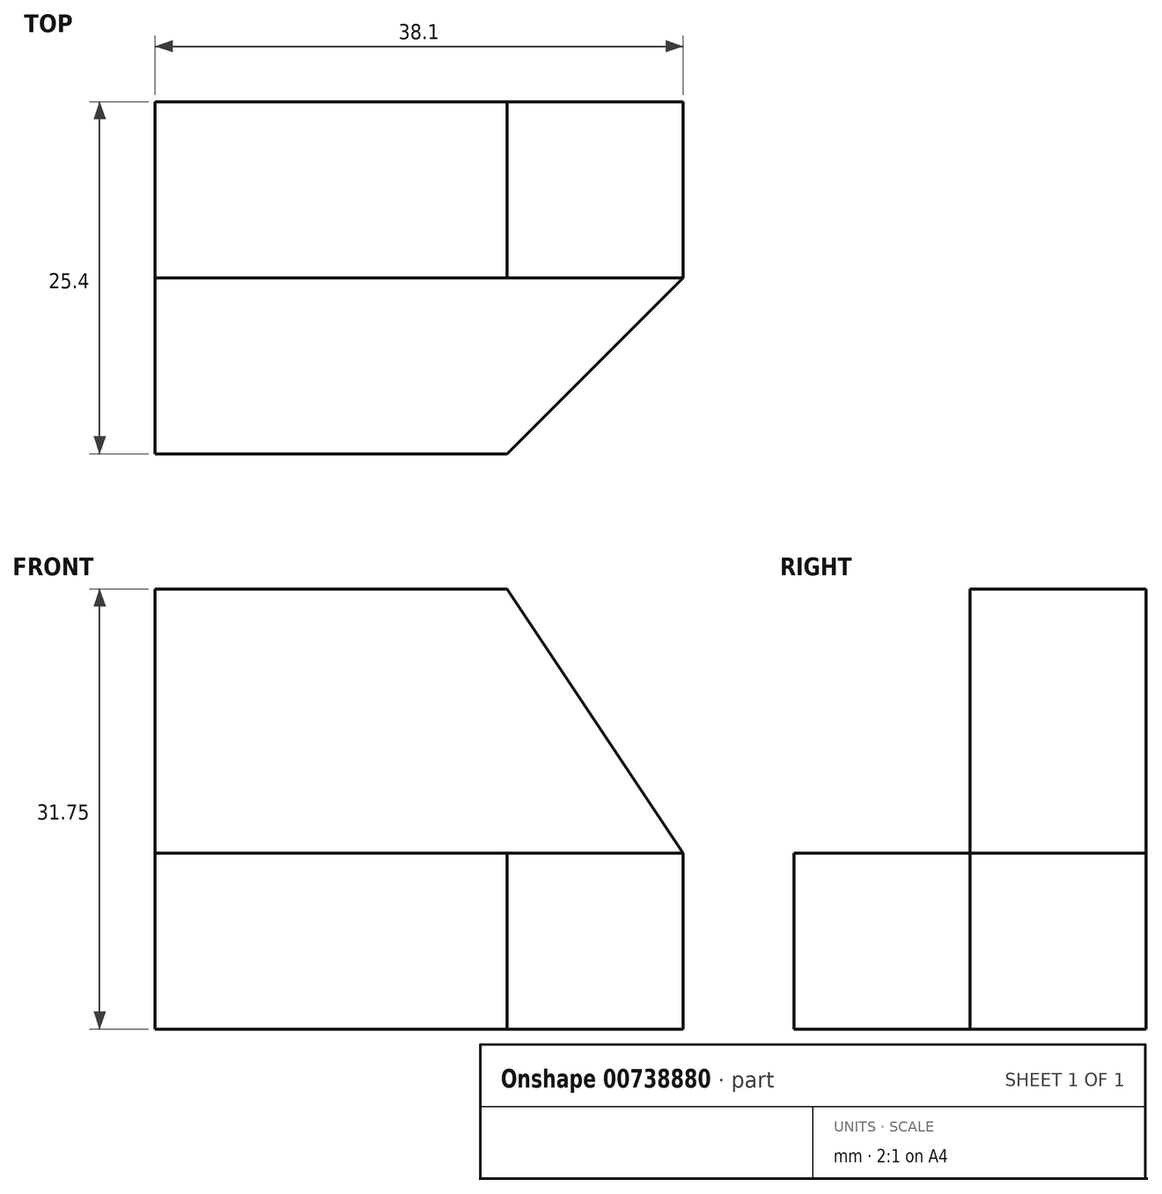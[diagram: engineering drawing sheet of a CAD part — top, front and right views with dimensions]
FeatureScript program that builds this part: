
annotation { "Feature Type Name" : "Feature", "Feature Type Description" : "" }
export const myFeature = defineFeature(function(context is Context, id is Id, definition is map)
    precondition{}
    {
        {
            var Q0;
            Q0=qCreatedBy(makeId("Front.planeOp"),FACE);
            var sketch = newSketch(context, id + "F0", { "sketchPlane" : qUnion([Q0])});
            skLineSegment(sketch, "E0", {"start": v(0, 0) * mm, "end": v(0, 31.75) * mm});
            skLineSegment(sketch, "E1", {"start": v(0, 31.75) * mm, "end": v(38.1, 31.75) * mm});
            skLineSegment(sketch, "E2", {"start": v(38.1, 31.75) * mm, "end": v(38.1, 0) * mm});
            skLineSegment(sketch, "E3", {"start": v(38.1, 0) * mm, "end": v(0, 0) * mm});
            skSolve(sketch);
        }
        {
            var Q0;
            Q0=makeQuery(id+"F0.imprint","IMPRINT",FACE,{"disambiguationData":[TD([[makeQuery(id+"F0.imprint","IMPRINT",EDGE,{"derivedFrom":sQuery(id+"F0.wireOp",EDGE,"E0")}),-1.0]])]});
            extrude(context, id + "F1", {"entities" : qUnion([Q0]), "depth" : 25.4 * mm, "offsetDistance" : 25.4 * mm});
        }
        {
            var Q0;
            Q0=makeQuery(id+"F1.opExtrude","SWEPT_FACE",FACE,{"disambiguationData":[OSD([sQuery(id+"F0.wireOp",EDGE,"E2")])]});
            var sketch = newSketch(context, id + "F2", { "sketchPlane" : qUnion([Q0])});
            skLineSegment(sketch, "E4", {"start": v(-12.7, 31.75) * mm, "end": v(-12.7, 12.7) * mm});
            skLineSegment(sketch, "E5", {"start": v(-12.7, 12.7) * mm, "end": v(-25.4, 12.7) * mm});
            skSolve(sketch);
        }
        {
            var Q0;
            Q0 = qSketchRegion(id + "F2", true);
            var Q1;
            {var subQ0=sQuery(id+"F2.wireOp",EDGE,"E4");Q1=makeQuery(id+"F2.imprint","IMPRINT",FACE,{"disambiguationData":[TD([[makeQuery(id+"F2.imprint","IMPRINT",EDGE,{"derivedFrom":subQ0}),-1.0]])]});}
            extrude(context, id + "F3", {"entities" : qUnion([Q0, Q1]), "operationType" : NewBodyOperationType.REMOVE, "endBound" : BoundingType.THROUGH_ALL, "oppositeDirection" : true, "depth" : 25.4 * mm, "offsetDistance" : 25.4 * mm});
        }
        {
            var Q0;
            Q0=makeQuery(id+"F3.boolean.opBoolean","COPY",FACE,{"derivedFrom":makeQuery(id+"F3.opExtrude","SWEPT_FACE",FACE,{"disambiguationData":[OSD([sQuery(id+"F2.wireOp",EDGE,"E4")])]})});
            var sketch = newSketch(context, id + "F4", { "sketchPlane" : qUnion([Q0])});
            skLineSegment(sketch, "E6", {"start": v(25.4, 31.75) * mm, "end": v(38.1, 12.7) * mm});
            skSolve(sketch);
        }
        {
            var Q0;
            Q0 = qSketchRegion(id + "F4", true);
            var Q1;
            {var subQ0=sQuery(id+"F4.wireOp",EDGE,"E6");Q1=makeQuery(id+"F4.imprint","IMPRINT",FACE,{"disambiguationData":[TD([[makeQuery(id+"F4.imprint","IMPRINT",EDGE,{"derivedFrom":subQ0}),1.0]])]});}
            extrude(context, id + "F5", {"entities" : qUnion([Q0, Q1]), "operationType" : NewBodyOperationType.REMOVE, "endBound" : BoundingType.THROUGH_ALL, "oppositeDirection" : true, "depth" : 25.4 * mm, "offsetDistance" : 25.4 * mm});
        }
        {
            var Q0;
            Q0=makeQuery(id+"F3.boolean.opBoolean","COPY",FACE,{"derivedFrom":makeQuery(id+"F3.opExtrude","SWEPT_FACE",FACE,{"disambiguationData":[OSD([sQuery(id+"F2.wireOp",EDGE,"E5")])]})});
            var sketch = newSketch(context, id + "F6", { "sketchPlane" : qUnion([Q0])});
            skLineSegment(sketch, "E7", {"start": v(38.1, -12.7) * mm, "end": v(25.4, -25.4) * mm});
            skSolve(sketch);
        }
        {
            var Q0;
            {var subQ0=sQuery(id+"F6.wireOp",EDGE,"E7");Q0=makeQuery(id+"F6.imprint","IMPRINT",FACE,{"disambiguationData":[TD([[makeQuery(id+"F6.imprint","IMPRINT",EDGE,{"derivedFrom":subQ0}),1.0]])]});}
            extrude(context, id + "F7", {"entities" : qUnion([Q0]), "operationType" : NewBodyOperationType.REMOVE, "endBound" : BoundingType.THROUGH_ALL, "oppositeDirection" : true, "depth" : 25.4 * mm, "offsetDistance" : 25.4 * mm});
        }
    });
